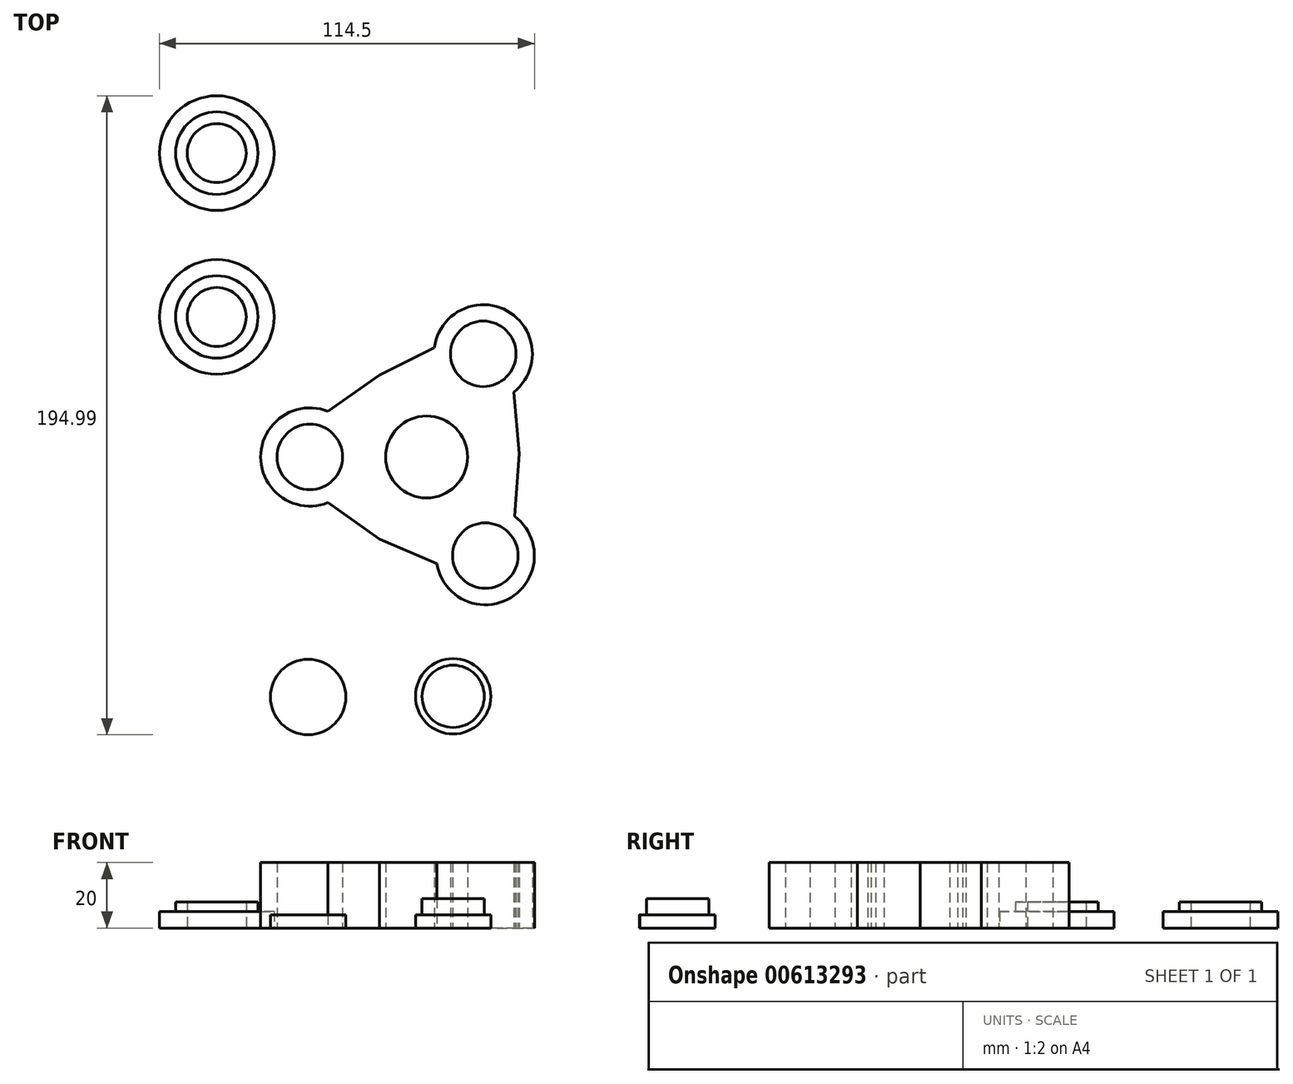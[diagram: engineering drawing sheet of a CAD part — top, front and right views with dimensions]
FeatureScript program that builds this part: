
annotation { "Feature Type Name" : "Feature", "Feature Type Description" : "" }
export const myFeature = defineFeature(function(context is Context, id is Id, definition is map)
    precondition{}
    {
        {
            var Q0;
            Q0=qCreatedBy(makeId("Top.planeOp"),FACE);
            var sketch = newSketch(context, id + "F0", { "sketchPlane" : qUnion([Q0])});
            skLineSegment(sketch, "E0.0", {"start": v(43.03, 16.36) * mm, "end": v(0.32, -9.64) * mm});
            skLineSegment(sketch, "E0.1", {"start": v(0.32, -9.64) * mm, "end": v(0.32, 40.36) * mm});
            skLineSegment(sketch, "E0.2", {"start": v(0.32, 40.36) * mm, "end": v(43.03, 16.36) * mm});
            skPoint(sketch, "E0.0.midPoint", {"position": v(21.67, 3.36) * mm});
            skCircle(sketch, "E1", {"center": v(32.7, -14.75) * mm, "radius": 10 * mm});
            skPoint(sketch, "E2.centerSnap0", {"position": v(0.32, 15.36) * mm});
            skCircle(sketch, "E3", {"center": v(-20.88, 15.36) * mm, "radius": 10 * mm});
            skLineSegment(sketch, "E4", {"start": v(-15.32, 29.3) * mm, "end": v(0.32, 40.36) * mm});
            skLineSegment(sketch, "E5", {"start": v(-15.32, 1.43) * mm, "end": v(0.32, -9.64) * mm});
            skLineSegment(sketch, "E6", {"start": v(17.9, -17.25) * mm, "end": v(0.32, -9.64) * mm});
            skLineSegment(sketch, "E7", {"start": v(41.7, -2.76) * mm, "end": v(43.03, 16.36) * mm});
            skCircle(sketch, "E8", {"center": v(32.7, -14.75) * mm, "radius": 15 * mm});
            skCircle(sketch, "E9", {"center": v(-20.88, 15.36) * mm, "radius": 15 * mm});
            skCircle(sketch, "E10", {"center": v(32.06, 46.84) * mm, "radius": 10 * mm});
            skCircle(sketch, "E11", {"center": v(32.06, 46.84) * mm, "radius": 15 * mm});
            skLineSegment(sketch, "E12", {"start": v(17.17, 48.69) * mm, "end": v(0.32, 40.36) * mm});
            skLineSegment(sketch, "E13", {"start": v(41.38, 35.09) * mm, "end": v(43.03, 16.36) * mm});
            skPoint(sketch, "E14.start.orphan", {"position": v(21.67, 28.36) * mm});
            skCircle(sketch, "E15", {"center": v(14.76, 15.36) * mm, "radius": 12.5 * mm});
            skSolve(sketch);
        }
        {
            var Q0;
            Q0=makeQuery(id+"F0.imprint","IMPRINT",FACE,{"disambiguationData":[TD([[makeQuery(id+"F0.imprint","IMPRINT",EDGE,{"derivedFrom":sQuery(id+"F0.wireOp",EDGE,"E0.0")}),-1.0]])]});
            var Q1;
            Q1=makeQuery(id+"F0.imprint","IMPRINT",FACE,{"disambiguationData":[TD([[makeQuery(id+"F0.imprint","IMPRINT",EDGE,{"derivedFrom":sQuery(id+"F0.wireOp",EDGE,"E0.0")}),1.0]])]});
            var Q2;
            Q2=makeQuery(id+"F0.imprint","IMPRINT",FACE,{"disambiguationData":[TD([[makeQuery(id+"F0.imprint","IMPRINT",EDGE,{"derivedFrom":sQuery(id+"F0.wireOp",EDGE,"E0.1")}),1.0]])]});
            var Q3;
            Q3=makeQuery(id+"F0.imprint","IMPRINT",FACE,{"disambiguationData":[TD([[makeQuery(id+"F0.imprint","IMPRINT",EDGE,{"derivedFrom":sQuery(id+"F0.wireOp",EDGE,"E0.2")}),1.0]])]});
            extrude(context, id + "F1", {"entities" : qUnion([Q0, Q1, Q2, Q3]), "depth" : 20 * mm, "offsetDistance" : 25 * mm});
        }
        {
            var Q0;
            Q0=makeQuery(id+"F0.imprint","IMPRINT",FACE,{"disambiguationData":[TD([[makeQuery(id+"F0.imprint","IMPRINT",EDGE,{"derivedFrom":sQuery(id+"F0.wireOp",EDGE,"E3")}),-1.0]])]});
            var Q1;
            Q1=makeQuery(id+"F0.imprint","IMPRINT",FACE,{"disambiguationData":[TD([[makeQuery(id+"F0.imprint","IMPRINT",EDGE,{"derivedFrom":sQuery(id+"F0.wireOp",EDGE,"E10")}),-1.0]])]});
            var Q2;
            Q2=makeQuery(id+"F0.imprint","IMPRINT",FACE,{"disambiguationData":[TD([[makeQuery(id+"F0.imprint","IMPRINT",EDGE,{"derivedFrom":sQuery(id+"F0.wireOp",EDGE,"E1")}),-1.0]])]});
            extrude(context, id + "F2", {"entities" : qUnion([Q0, Q1, Q2]), "operationType" : NewBodyOperationType.ADD, "depth" : 20 * mm, "offsetDistance" : 25 * mm});
        }
        {
            var Q0;
            Q0=qCreatedBy(makeId("Top.planeOp"),FACE);
            var sketch = newSketch(context, id + "F3", { "sketchPlane" : qUnion([Q0])});
            skCircle(sketch, "E16", {"center": v(-49.3, 58.09) * mm, "radius": 12.6 * mm});
            skCircle(sketch, "E17", {"center": v(-49.3, 58.09) * mm, "radius": 9 * mm});
            skCircle(sketch, "E18", {"center": v(-49.3, 58.09) * mm, "radius": 17.5 * mm});
            skSolve(sketch);
        }
        {
            var Q0;
            Q0 = qSketchRegion(id + "F3", true);
            extrude(context, id + "F4", {"entities" : qUnion([Q0]), "depth" : 5 * mm, "offsetDistance" : 25 * mm});
        }
        {
            var Q0;
            Q0=makeQuery(id+"F3.imprint","IMPRINT",FACE,{"disambiguationData":[TD([[makeQuery(id+"F3.imprint","IMPRINT",EDGE,{"derivedFrom":sQuery(id+"F3.wireOp",EDGE,"E16")}),1.0]])]});
            extrude(context, id + "F5", {"entities" : qUnion([Q0]), "operationType" : NewBodyOperationType.ADD, "depth" : 8 * mm, "offsetDistance" : 25 * mm});
        }
        {
            var Q0;
            Q0=makeQuery(id+"F4.opExtrude","SWEPT_BODY",BODY,{"disambiguationData":[OSD([sQuery(id+"F3.wireOp",EDGE,"E16"),sQuery(id+"F3.wireOp",EDGE,"E18")])]});
            transform(context, id + "F6", {"entities" : qUnion([Q0]), "transformType" : TransformType.TRANSLATION_3D, "dx" : 0 * mm, "dy" : 50 * mm, "dz" : 0 * mm, "makeCopy" : true});
        }
        {
            var Q0;
            Q0=qCreatedBy(makeId("Top.planeOp"),FACE);
            var sketch = newSketch(context, id + "F7", { "sketchPlane" : qUnion([Q0])});
            skCircle(sketch, "E19", {"center": v(22.87, -57.7) * mm, "radius": 11.5 * mm});
            skCircle(sketch, "E20", {"center": v(22.87, -57.7) * mm, "radius": 9.5 * mm});
            skSolve(sketch);
        }
        {
            var Q0;
            Q0=qCreatedBy(makeId("Top.planeOp"),FACE);
            var sketch = newSketch(context, id + "F8", { "sketchPlane" : qUnion([Q0])});
            skCircle(sketch, "E21", {"center": v(-21.4, -57.9) * mm, "radius": 11.5 * mm});
            skSolve(sketch);
        }
        {
            var Q0;
            Q0=makeQuery(id+"F7.imprint","IMPRINT",FACE,{"disambiguationData":[TD([[makeQuery(id+"F7.imprint","IMPRINT",EDGE,{"derivedFrom":sQuery(id+"F7.wireOp",EDGE,"E20")}),1.0]])]});
            extrude(context, id + "F9", {"entities" : qUnion([Q0]), "depth" : 9 * mm, "offsetDistance" : 25 * mm});
        }
        {
            var Q0;
            Q0=makeQuery(id+"F7.imprint","IMPRINT",FACE,{"disambiguationData":[TD([[makeQuery(id+"F7.imprint","IMPRINT",EDGE,{"derivedFrom":sQuery(id+"F7.wireOp",EDGE,"E19")}),1.0]])]});
            extrude(context, id + "F10", {"entities" : qUnion([Q0]), "operationType" : NewBodyOperationType.ADD, "depth" : 4 * mm, "offsetDistance" : 25 * mm});
        }
        {
            var Q0;
            Q0=makeQuery(id+"F8.imprint","IMPRINT",FACE,{"disambiguationData":[TD([[makeQuery(id+"F8.imprint","IMPRINT",EDGE,{"derivedFrom":sQuery(id+"F8.wireOp",EDGE,"E21")}),1.0]])]});
            extrude(context, id + "F11", {"entities" : qUnion([Q0]), "depth" : 4 * mm, "offsetDistance" : 25 * mm});
        }
    });
